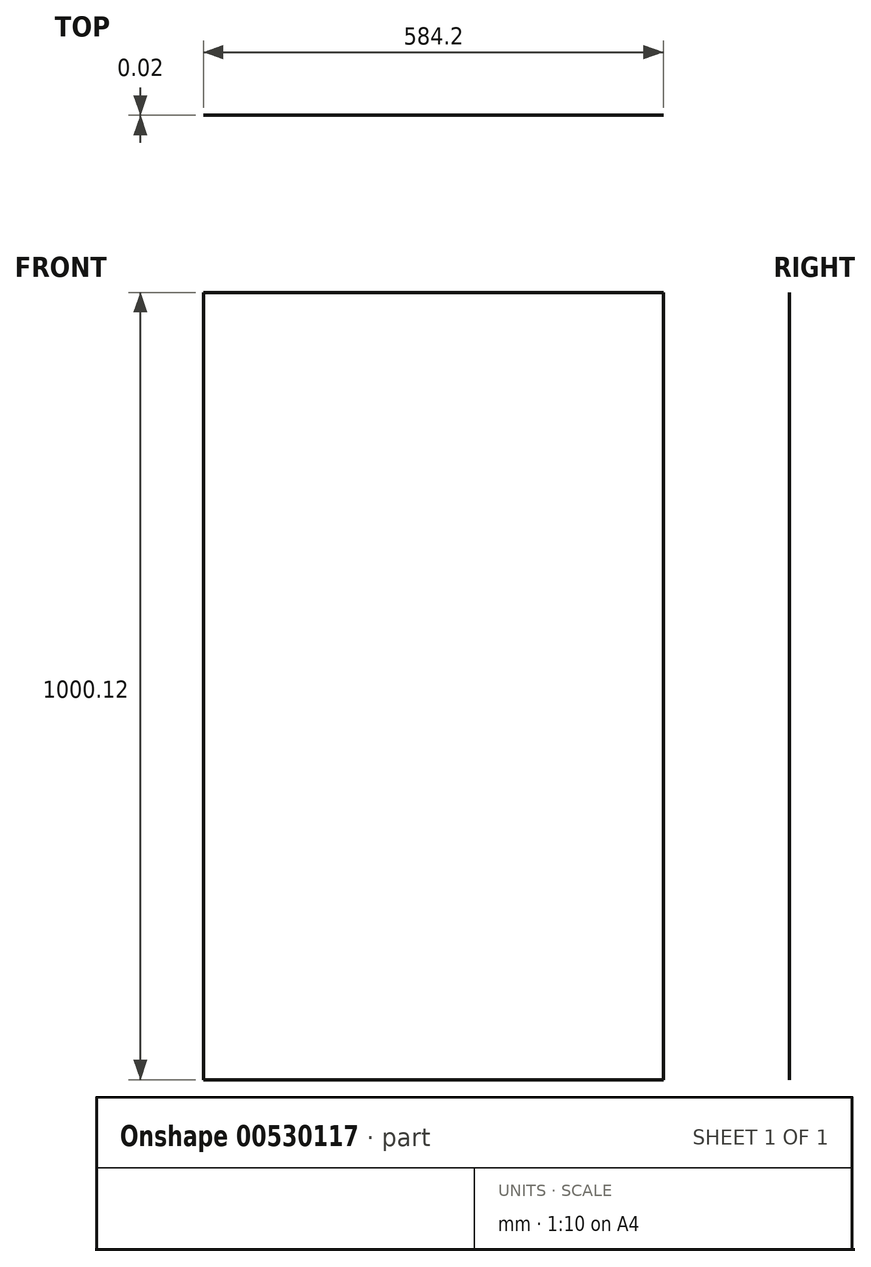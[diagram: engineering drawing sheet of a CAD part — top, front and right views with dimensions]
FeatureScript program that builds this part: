
annotation { "Feature Type Name" : "Feature", "Feature Type Description" : "" }
export const myFeature = defineFeature(function(context is Context, id is Id, definition is map)
    precondition{}
    {
        {
            var Q0;
            Q0=qCreatedBy(makeId("Front.planeOp"),FACE);
            var sketch = newSketch(context, id + "F0", { "sketchPlane" : qUnion([Q0])});
            skLineSegment(sketch, "E0.bottom", {"start": v(-292.1, -500.06) * mm, "end": v(292.1, -500.06) * mm});
            skLineSegment(sketch, "E0.top", {"start": v(-292.1, 500.06) * mm, "end": v(292.1, 500.06) * mm});
            skLineSegment(sketch, "E0.left", {"start": v(-292.1, -500.06) * mm, "end": v(-292.1, 500.06) * mm});
            skLineSegment(sketch, "E0.right", {"start": v(292.1, -500.06) * mm, "end": v(292.1, 500.06) * mm});
            skPoint(sketch, "E0.middle", {"position": v(0, 0) * mm});
            skSolve(sketch);
        }
        {
            var Q0;
            Q0=makeQuery(id+"F0.imprint","IMPRINT",FACE,{"disambiguationData":[TD([[makeQuery(id+"F0.imprint","IMPRINT",EDGE,{"derivedFrom":sQuery(id+"F0.wireOp",EDGE,"E0.bottom")}),1.0]])]});
            extrude(context, id + "F1", {"entities" : qUnion([Q0]), "endBound" : BoundingType.SYMMETRIC, "depth" : 5 / 203.2 * mm, "offsetDistance" : 25.4 * mm});
        }
    });
